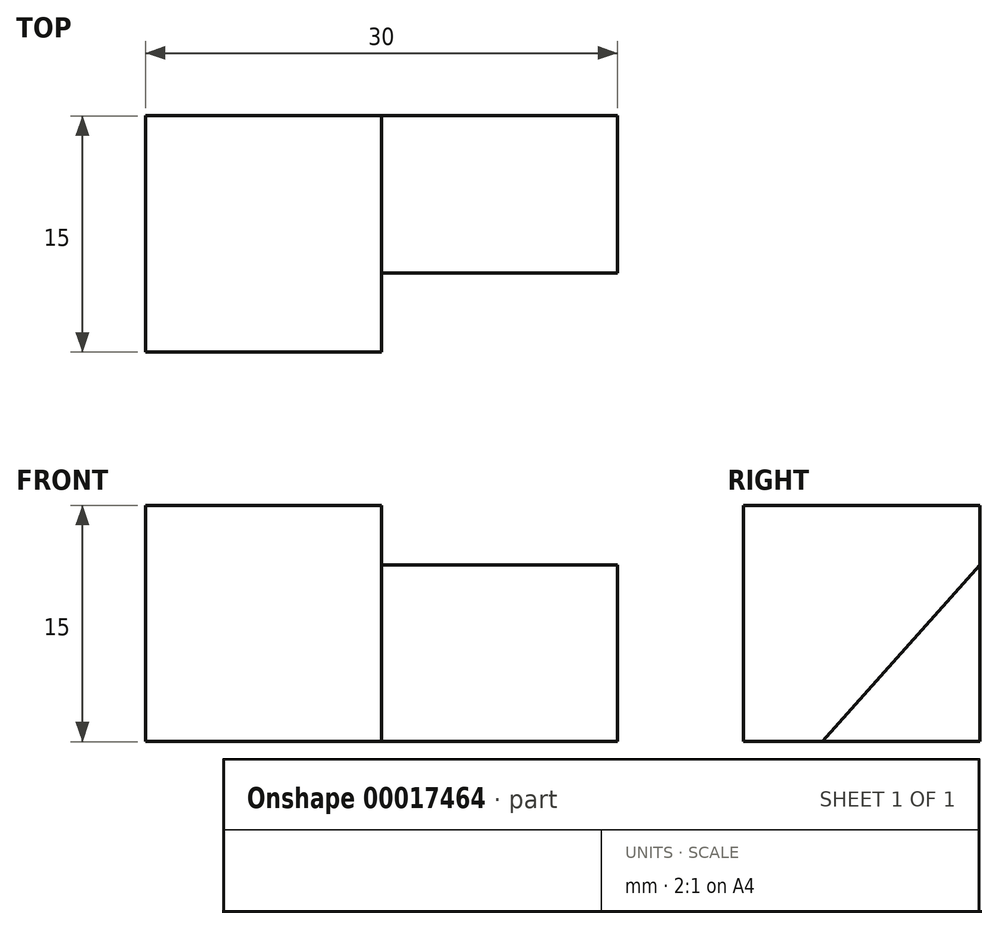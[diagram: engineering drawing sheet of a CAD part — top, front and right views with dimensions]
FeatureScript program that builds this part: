
annotation { "Feature Type Name" : "Feature", "Feature Type Description" : "" }
export const myFeature = defineFeature(function(context is Context, id is Id, definition is map)
    precondition{}
    {
        {
            var Q0;
            Q0=qCreatedBy(makeId("Right.planeOp"),FACE);
            var sketch = newSketch(context, id + "F0", { "sketchPlane" : qUnion([Q0])});
            skLineSegment(sketch, "E0", {"start": v(-0.65, 3.78) * mm, "end": v(-0.65, -11.22) * mm});
            skLineSegment(sketch, "E1", {"start": v(-0.65, -11.22) * mm, "end": v(14.35, -11.22) * mm});
            skLineSegment(sketch, "E2", {"start": v(14.35, -11.22) * mm, "end": v(14.35, 3.78) * mm});
            skLineSegment(sketch, "E3", {"start": v(14.35, 3.78) * mm, "end": v(-0.65, 3.78) * mm});
            skSolve(sketch);
        }
        {
            var Q0;
            Q0=makeQuery(id+"F0.imprint","IMPRINT",FACE,{"disambiguationData":[TD([[makeQuery(id+"F0.imprint","IMPRINT",EDGE,{"derivedFrom":sQuery(id+"F0.wireOp",EDGE,"E0")}),1.0]])]});
            extrude(context, id + "F1", {"entities" : qUnion([Q0]), "oppositeDirection" : true, "depth" : 15 * mm});
        }
        {
            var Q0;
            Q0=makeQuery(id+"F1.opExtrude","CAP_FACE",FACE,{"disambiguationData":[OSD([sQuery(id+"F0.wireOp",EDGE,"E0"),sQuery(id+"F0.wireOp",EDGE,"E1"),sQuery(id+"F0.wireOp",EDGE,"E2"),sQuery(id+"F0.wireOp",EDGE,"E3")])],"isStart":true});
            var sketch = newSketch(context, id + "F2", { "sketchPlane" : qUnion([Q0])});
            skLineSegment(sketch, "E4", {"start": v(14.35, -11.22) * mm, "end": v(14.35, 0) * mm});
            skLineSegment(sketch, "E5", {"start": v(14.35, 0) * mm, "end": v(4.35, -11.22) * mm});
            skLineSegment(sketch, "E6", {"start": v(4.35, -11.22) * mm, "end": v(14.35, -11.22) * mm});
            skLineSegment(sketch, "E7", {"start": v(14.35, 0) * mm, "end": v(14.35, -11.22) * mm});
            skSolve(sketch);
        }
        {
            var Q0;
            Q0 = qSketchRegion(id + "F2", true);
            extrude(context, id + "F3", {"entities" : qUnion([Q0]), "operationType" : NewBodyOperationType.ADD, "depth" : 15 * mm});
        }
    });
